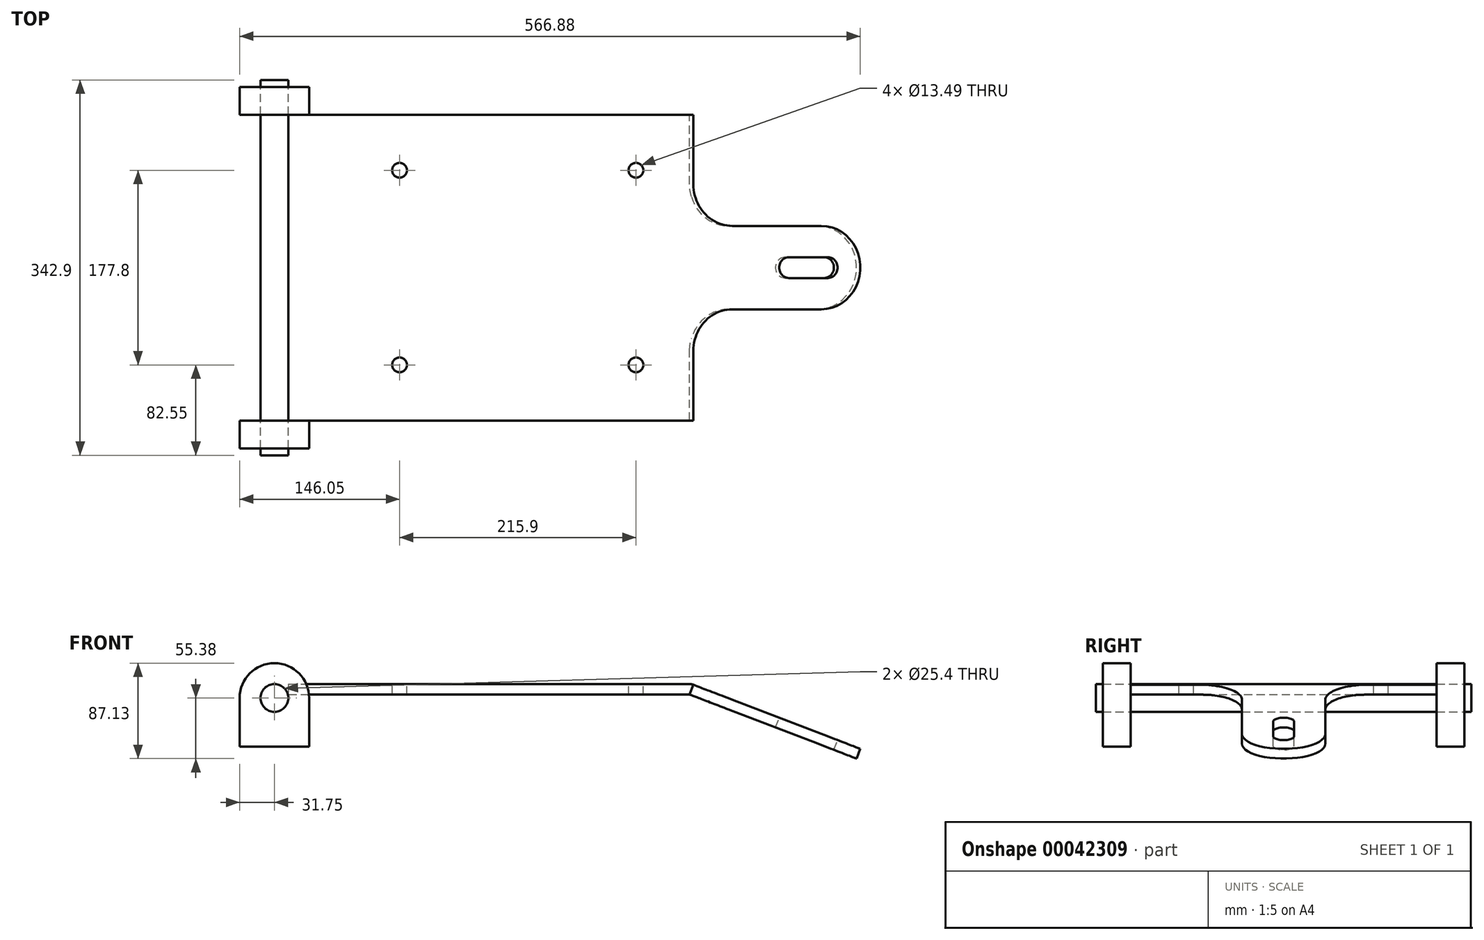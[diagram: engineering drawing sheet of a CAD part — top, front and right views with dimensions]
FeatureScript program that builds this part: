
annotation { "Feature Type Name" : "Feature", "Feature Type Description" : "" }
export const myFeature = defineFeature(function(context is Context, id is Id, definition is map)
    precondition{}
    {
        {
            var Q0;
            Q0=qCreatedBy(makeId("Front.planeOp"),FACE);
            var sketch = newSketch(context, id + "F0", { "sketchPlane" : qUnion([Q0])});
            skLineSegment(sketch, "E0", {"start": v(-368.3, 0) * mm, "end": v(-1.77, 0) * mm});
            skLineSegment(sketch, "E1", {"start": v(1.65, -0.63) * mm, "end": v(154.13, -59.19) * mm});
            skLineSegment(sketch, "E2.0", {"start": v(-0.12, -10.16) * mm, "end": v(150.71, -68.08) * mm});
            skLineSegment(sketch, "E2.1", {"start": v(-368.3, -9.53) * mm, "end": v(-3.53, -9.53) * mm});
            skLineSegment(sketch, "E3", {"start": v(-368.3, 0) * mm, "end": v(-368.3, -9.53) * mm});
            skLineSegment(sketch, "E4", {"start": v(154.13, -59.19) * mm, "end": v(150.71, -68.08) * mm});
            skPoint(sketch, "E5.visualSharp", {"position": v(0, 0) * mm});
            skArc(sketch, "E5.filletArc", {"start": v(1.65, -0.63) * mm, "mid": v(-0.03, -0.16) * mm, "end": v(-1.77, 0) * mm});
            skArc(sketch, "E6.filletArc", {"start": v(-0.12, -10.16) * mm, "mid": v(-1.8, -9.68) * mm, "end": v(-3.53, -9.52) * mm});
            skSolve(sketch);
        }
        {
            var Q0;
            Q0=makeQuery(id+"F0.imprint","IMPRINT",FACE,{"disambiguationData":[TD([[makeQuery(id+"F0.imprint","IMPRINT",EDGE,{"derivedFrom":sQuery(id+"F0.wireOp",EDGE,"E0")}),-1.0]])]});
            extrude(context, id + "F1", {"entities" : qUnion([Q0]), "depth" : 279.4 * mm});
        }
        {
            var Q0;
            Q0=makeQuery(id+"F1.opExtrude","SWEPT_FACE",FACE,{"disambiguationData":[OSD([sQuery(id+"F0.wireOp",EDGE,"E1")])]});
            var sketch = newSketch(context, id + "F2", { "sketchPlane" : qUnion([Q0])});
            skLineSegment(sketch, "E7", {"start": v(286.09, -139.7) * mm, "end": v(-117.54, -139.7) * mm, "construction": true});
            skPoint(sketch, "E7.startSnap0", {"position": v(165.1, -139.7) * mm});
            skLineSegment(sketch, "E8", {"start": v(39.87, -101.6) * mm, "end": v(127, -101.6) * mm});
            skLineSegment(sketch, "E9.MirrorCS", {"start": v(39.87, -177.8) * mm, "end": v(127, -177.8) * mm});
            skLineSegment(sketch, "E10", {"start": v(1.77, -63.5) * mm, "end": v(1.77, 0) * mm});
            skLineSegment(sketch, "E11", {"start": v(1.77, -215.9) * mm, "end": v(1.77, -279.4) * mm});
            skLineSegment(sketch, "E12", {"start": v(165.1, -139.7) * mm, "end": v(165.1, -139.7) * mm});
            skPoint(sketch, "E13.visualSharp", {"position": v(1.77, -101.6) * mm});
            skArc(sketch, "E13.filletArc", {"start": v(1.77, -63.5) * mm, "mid": v(12.93, -90.44) * mm, "end": v(39.87, -101.6) * mm});
            skPoint(sketch, "E14.visualSharp", {"position": v(165.1, -101.6) * mm});
            skArc(sketch, "E14.filletArc", {"start": v(165.1, -139.7) * mm, "mid": v(153.94, -112.76) * mm, "end": v(127, -101.6) * mm});
            skPoint(sketch, "E15.visualSharp", {"position": v(165.1, -177.8) * mm});
            skArc(sketch, "E15.filletArc", {"start": v(127, -177.8) * mm, "mid": v(153.94, -166.64) * mm, "end": v(165.1, -139.7) * mm});
            skPoint(sketch, "E16.visualSharp", {"position": v(1.77, -177.8) * mm});
            skArc(sketch, "E16.filletArc", {"start": v(39.87, -177.8) * mm, "mid": v(12.93, -188.96) * mm, "end": v(1.77, -215.9) * mm});
            skLineSegment(sketch, "E17", {"start": v(133.35, -139.7) * mm, "end": v(95.25, -139.7) * mm});
            skArc(sketch, "E18.0.startCap", {"start": v(133.35, -130.17) * mm, "mid": v(142.88, -139.7) * mm, "end": v(133.35, -149.22) * mm});
            skArc(sketch, "E18.0.endCap", {"start": v(95.25, -149.22) * mm, "mid": v(85.73, -139.7) * mm, "end": v(95.25, -130.17) * mm});
            skLineSegment(sketch, "E18.0.left", {"start": v(133.35, -149.22) * mm, "end": v(95.25, -149.22) * mm});
            skLineSegment(sketch, "E18.0.right", {"start": v(133.35, -130.17) * mm, "end": v(95.25, -130.17) * mm});
            skSolve(sketch);
        }
        {
            var Q0;
            Q0 = qSketchRegion(id + "F2", true);
            var Q1;
            Q1=makeQuery(id+"F2.imprint","IMPRINT",FACE,{"disambiguationData":[TD([[makeQuery(id+"F2.imprint","IMPRINT",EDGE,{"derivedFrom":sQuery(id+"F2.wireOp",EDGE,"E9.MirrorCS")}),-1.0]])]});
            var Q2;
            Q2=makeQuery(id+"F2.imprint","IMPRINT",FACE,{"disambiguationData":[TD([[makeQuery(id+"F2.imprint","IMPRINT",EDGE,{"derivedFrom":sQuery(id+"F2.wireOp",EDGE,"E8")}),1.0]])]});
            extrude(context, id + "F3", {"entities" : qUnion([Q0, Q1, Q2]), "operationType" : NewBodyOperationType.REMOVE, "oppositeDirection" : true, "depth" : 25.4 * mm});
        }
        {
            var Q0;
            Q0=makeQuery(id+"F1.opExtrude","SWEPT_FACE",FACE,{"disambiguationData":[OSD([sQuery(id+"F0.wireOp",EDGE,"E0")])]});
            var sketch = newSketch(context, id + "F4", { "sketchPlane" : qUnion([Q0])});
            skLineSegment(sketch, "E19", {"start": v(-405.03, -139.7) * mm, "end": v(209, -139.7) * mm, "construction": true});
            skPoint(sketch, "E19.startSnap0", {"position": v(-368.3, -139.7) * mm});
            skLineSegment(sketch, "E20", {"start": v(-50.8, 0) * mm, "end": v(-50.8, -139.7) * mm, "construction": true});
            skLineSegment(sketch, "E21", {"start": v(-266.7, 0) * mm, "end": v(-266.7, -139.7) * mm, "construction": true});
            skLineSegment(sketch, "E22", {"start": v(-368.3, -50.8) * mm, "end": v(-1.77, -50.8) * mm, "construction": true});
            skLineSegment(sketch, "E23.MirrorCS", {"start": v(-266.7, -279.4) * mm, "end": v(-266.7, -139.7) * mm, "construction": true});
            skLineSegment(sketch, "E24.MirrorCS", {"start": v(-368.3, -228.6) * mm, "end": v(-1.77, -228.6) * mm, "construction": true});
            skLineSegment(sketch, "E25.MirrorCS", {"start": v(-50.8, -279.4) * mm, "end": v(-50.8, -139.7) * mm, "construction": true});
            skPoint(sketch, "E26", {"position": v(-266.7, -50.8) * mm});
            skPoint(sketch, "E27", {"position": v(-266.7, -228.6) * mm});
            skPoint(sketch, "E28", {"position": v(-50.8, -228.6) * mm});
            skPoint(sketch, "E29", {"position": v(-50.8, -50.8) * mm});
            skSolve(sketch);
        }
        {
            var Q0;
            Q0=sQuery(id+"F4.wireOp",VERTEX,"E27");
            var Q1;
            Q1=sQuery(id+"F4.wireOp",VERTEX,"E26");
            var Q2;
            Q2=sQuery(id+"F4.wireOp",VERTEX,"E29");
            var Q3;
            Q3=sQuery(id+"F4.wireOp",VERTEX,"E28");
            var Q4;
            Q4=makeQuery(id+"F1.opExtrude","SWEPT_BODY",BODY,{"disambiguationData":[OSD([sQuery(id+"F0.wireOp",EDGE,"E0"),sQuery(id+"F0.wireOp",EDGE,"E1"),sQuery(id+"F0.wireOp",EDGE,"E2.0"),sQuery(id+"F0.wireOp",EDGE,"E2.1"),sQuery(id+"F0.wireOp",EDGE,"E3"),sQuery(id+"F0.wireOp",EDGE,"E4"),sQuery(id+"F0.wireOp",EDGE,"E5.filletArc"),sQuery(id+"F0.wireOp",EDGE,"E6.filletArc")])]});
            hole(context, id + "F5", {"style" : HoleStyle.SIMPLE, "holeDiameter" : 13.5 * mm, "endStyle" : HoleEndStyle.THROUGH, "locations" : qUnion([Q0, Q1, Q2, Q3]), "scope" : qUnion([Q4])});
        }
        {
            var Q0;
            Q0=qCreatedBy(makeId("Front.planeOp"),FACE);
            cPlane(context, id + "F6", {"entities" : qUnion([Q0]), "cplaneType" : CPlaneType.OFFSET, "offset" : 139.7 * mm, "width" : 152.4 * mm, "height" : 152.4 * mm});
        }
        {
            var Q0;
            Q0=qCreatedBy(id+"F6.planeOp",FACE);
            var sketch = newSketch(context, id + "F7", { "sketchPlane" : qUnion([Q0])});
            skLineSegment(sketch, "E30.0", {"start": v(-368.3, 0) * mm, "end": v(-1.77, 0) * mm, "construction": true});
            skLineSegment(sketch, "E31", {"start": v(-368.3, 0) * mm, "end": v(-381, 0) * mm, "construction": true});
            skLineSegment(sketch, "E32", {"start": v(-381, 0) * mm, "end": v(-381, -12.7) * mm, "construction": true});
            skCircle(sketch, "E33", {"center": v(-381, -12.7) * mm, "radius": 12.7 * mm});
            skSolve(sketch);
        }
        {
            var Q0;
            Q0 = qSketchRegion(id + "F7", true);
            extrude(context, id + "F8", {"entities" : qUnion([Q0]), "endBound" : BoundingType.SYMMETRIC, "depth" : 342.9 * mm});
        }
        {
            var Q0;
            Q0=makeQuery(id+"F1.opExtrude","CAP_FACE",FACE,{"disambiguationData":[OSD([sQuery(id+"F0.wireOp",EDGE,"E0"),sQuery(id+"F0.wireOp",EDGE,"E1"),sQuery(id+"F0.wireOp",EDGE,"E2.0"),sQuery(id+"F0.wireOp",EDGE,"E2.1"),sQuery(id+"F0.wireOp",EDGE,"E3"),sQuery(id+"F0.wireOp",EDGE,"E4"),sQuery(id+"F0.wireOp",EDGE,"E5.filletArc"),sQuery(id+"F0.wireOp",EDGE,"E6.filletArc")])],"isStart":false});
            var sketch = newSketch(context, id + "F9", { "sketchPlane" : qUnion([Q0])});
            skCircle(sketch, "E34.0", {"center": v(-381, -12.7) * mm, "radius": 12.7 * mm});
            skLineSegment(sketch, "E35.rect.bottom", {"start": v(-412.75, -57.15) * mm, "end": v(-349.25, -57.15) * mm});
            skLineSegment(sketch, "E35.rect.left", {"start": v(-412.75, -57.15) * mm, "end": v(-412.75, -12.7) * mm});
            skLineSegment(sketch, "E35.rect.right", {"start": v(-349.25, -57.15) * mm, "end": v(-349.25, -12.7) * mm});
            skLineSegment(sketch, "E36", {"start": v(-412.75, -12.7) * mm, "end": v(-349.25, -12.7) * mm, "construction": true});
            skArc(sketch, "E37", {"start": v(-349.25, -12.7) * mm, "mid": v(-381, 19.05) * mm, "end": v(-412.75, -12.7) * mm});
            skLineSegment(sketch, "E38", {"start": v(-381, -12.7) * mm, "end": v(-381, 19.05) * mm, "construction": true});
            skSolve(sketch);
        }
        {
            var Q0;
            Q0 = qSketchRegion(id + "F9", true);
            extrude(context, id + "F10", {"entities" : qUnion([Q0]), "depth" : 25.4 * mm});
        }
        {
            var Q0;
            Q0=makeQuery(id+"F10.opExtrude","SWEPT_BODY",BODY,{"disambiguationData":[OSD([sQuery(id+"F9.wireOp",EDGE,"E34.0"),sQuery(id+"F9.wireOp",EDGE,"E35.rect.bottom"),sQuery(id+"F9.wireOp",EDGE,"E35.rect.left"),sQuery(id+"F9.wireOp",EDGE,"E35.rect.right"),sQuery(id+"F9.wireOp",EDGE,"E37")])]});
            transform(context, id + "F11", {"entities" : qUnion([Q0]), "transformType" : TransformType.TRANSLATION_3D, "dx" : 0 * mm, "dy" : 304.8 * mm, "dz" : 0 * mm, "makeCopy" : true});
        }
    });
